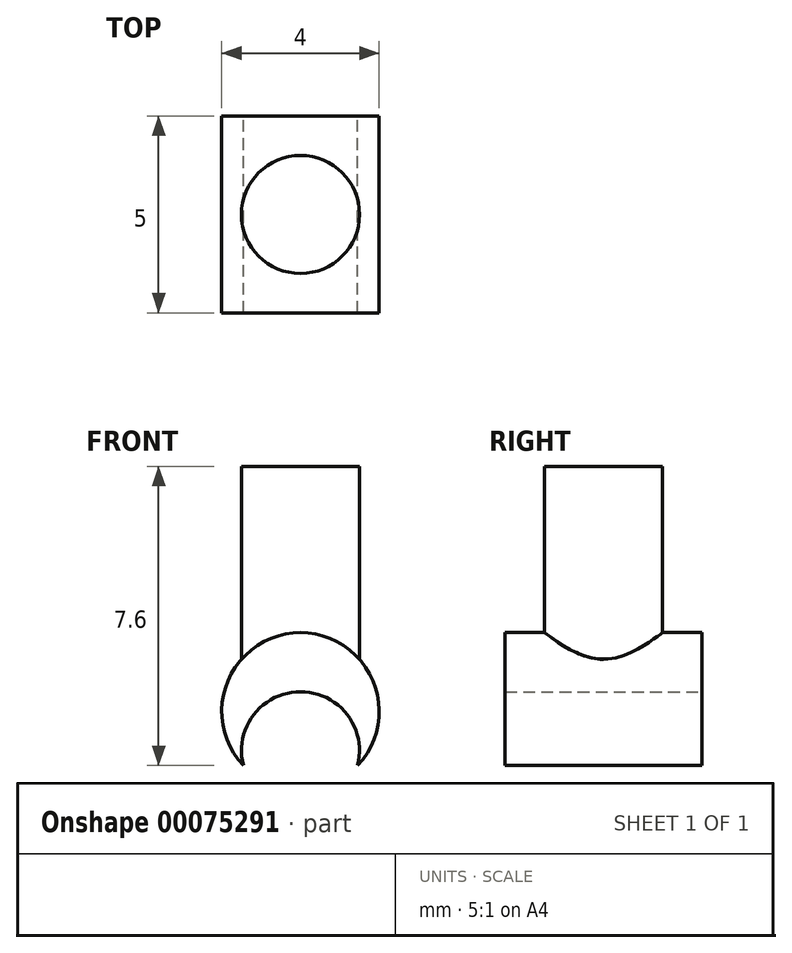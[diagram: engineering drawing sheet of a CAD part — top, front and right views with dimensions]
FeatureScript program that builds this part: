
annotation { "Feature Type Name" : "Feature", "Feature Type Description" : "" }
export const myFeature = defineFeature(function(context is Context, id is Id, definition is map)
    precondition{}
    {
        {
            var Q0;
            Q0=qCreatedBy(makeId("Front.planeOp"),FACE);
            var sketch = newSketch(context, id + "F0", { "sketchPlane" : qUnion([Q0])});
            skArc(sketch, "E0", {"start": v(1.45, -2.6) * mm, "mid": v(0, 0.77) * mm, "end": v(-1.45, -2.6) * mm});
            skArc(sketch, "E1", {"start": v(1.45, -2.6) * mm, "mid": v(0, -0.73) * mm, "end": v(-1.45, -2.6) * mm});
            skSolve(sketch);
        }
        {
            var Q0;
            Q0 = qSketchRegion(id + "F0", true);
            extrude(context, id + "F1", {"entities" : qUnion([Q0]), "endBound" : BoundingType.SYMMETRIC, "depth" : 5 * mm});
        }
        {
            var Q0;
            Q0=qCreatedBy(makeId("Top.planeOp"),FACE);
            var sketch = newSketch(context, id + "F2", { "sketchPlane" : qUnion([Q0])});
            skCircle(sketch, "E2", {"center": v(0, 0) * mm, "radius": 1.5 * mm});
            skSolve(sketch);
        }
        {
            var Q0;
            Q0 = qSketchRegion(id + "F2", true);
            extrude(context, id + "F3", {"entities" : qUnion([Q0]), "operationType" : NewBodyOperationType.ADD, "depth" : 5 * mm});
        }
    });
